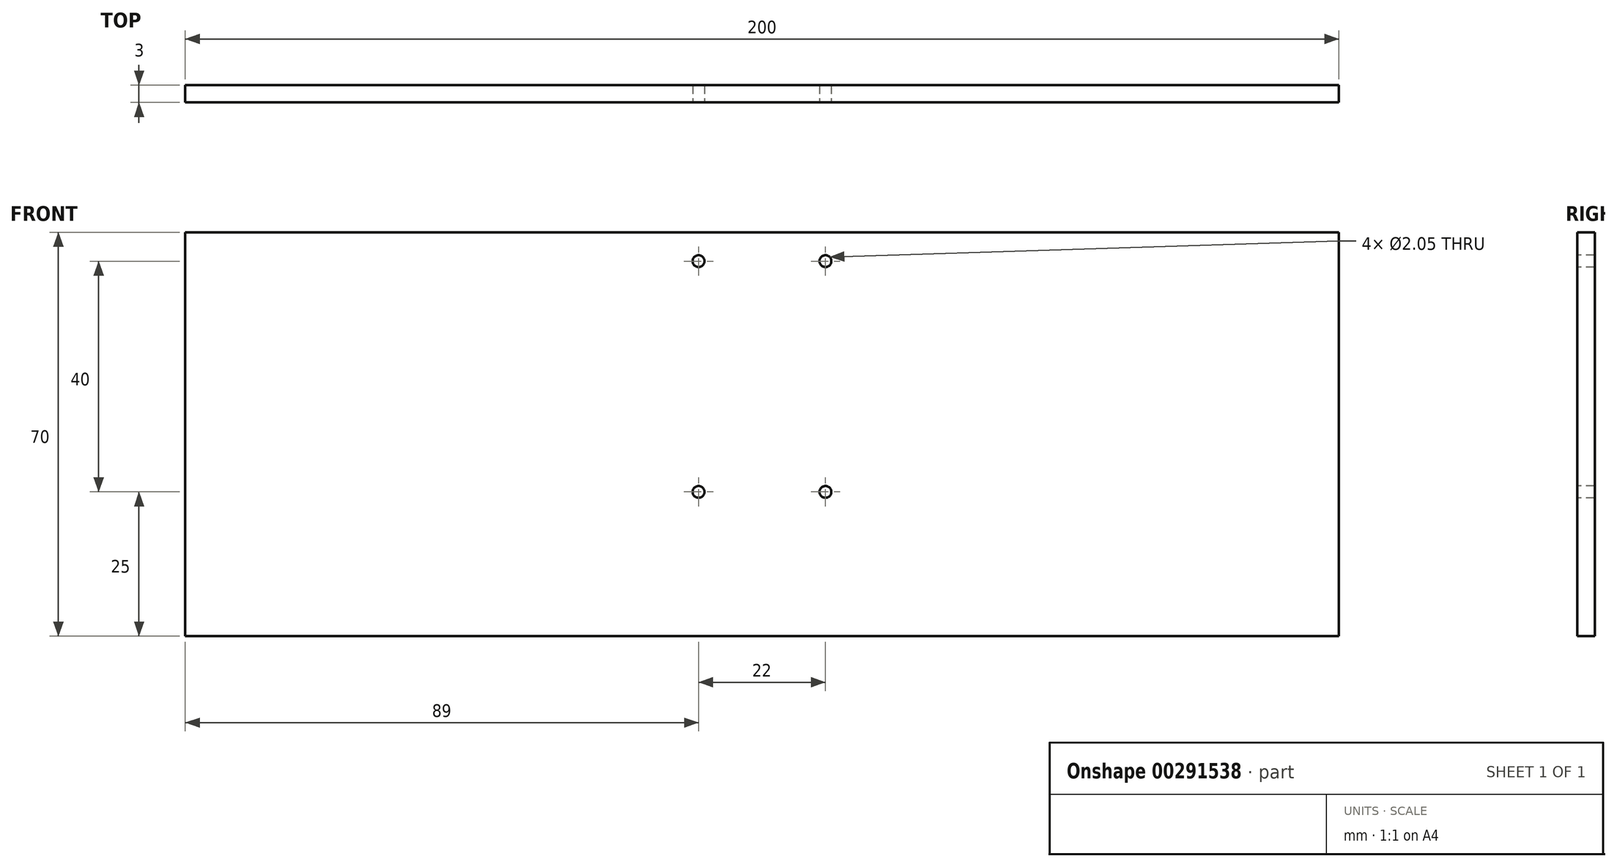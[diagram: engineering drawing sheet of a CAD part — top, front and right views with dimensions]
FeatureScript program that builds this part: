
annotation { "Feature Type Name" : "Feature", "Feature Type Description" : "" }
export const myFeature = defineFeature(function(context is Context, id is Id, definition is map)
    precondition{}
    {
        {
            var Q0;
            Q0=qCreatedBy(makeId("Front.planeOp"),FACE);
            var sketch = newSketch(context, id + "F0", { "sketchPlane" : qUnion([Q0])});
            skLineSegment(sketch, "E0.bottom", {"start": v(-100, 25) * mm, "end": v(100, 25) * mm});
            skLineSegment(sketch, "E0.top", {"start": v(-100, -45) * mm, "end": v(100, -45) * mm});
            skLineSegment(sketch, "E0.left", {"start": v(-100, 25) * mm, "end": v(-100, -45) * mm});
            skLineSegment(sketch, "E0.right", {"start": v(100, 25) * mm, "end": v(100, -45) * mm});
            skSolve(sketch);
        }
        {
            var Q0;
            Q0=makeQuery(id+"F0.imprint","IMPRINT",FACE,{"disambiguationData":[TD([[makeQuery(id+"F0.imprint","IMPRINT",EDGE,{"derivedFrom":sQuery(id+"F0.wireOp",EDGE,"E0.bottom")}),-1.0]])]});
            extrude(context, id + "F1", {"entities" : qUnion([Q0]), "endBound" : BoundingType.SYMMETRIC, "depth" : 3 * mm});
        }
        {
            var Q0;
            Q0=makeQuery(id+"F1.opExtrude","CAP_FACE",FACE,{"disambiguationData":[OSD([sQuery(id+"F0.wireOp",EDGE,"E0.bottom"),sQuery(id+"F0.wireOp",EDGE,"E0.top"),sQuery(id+"F0.wireOp",EDGE,"E0.left"),sQuery(id+"F0.wireOp",EDGE,"E0.right")])],"isStart":false});
            var sketch = newSketch(context, id + "F2", { "sketchPlane" : qUnion([Q0])});
            skCircle(sketch, "E1", {"center": v(-11, 20) * mm, "radius": 1.02 * mm});
            skCircle(sketch, "E2", {"center": v(11, 20) * mm, "radius": 1.02 * mm});
            skCircle(sketch, "E3", {"center": v(11, -20) * mm, "radius": 1.02 * mm});
            skCircle(sketch, "E4", {"center": v(-11, -20) * mm, "radius": 1.02 * mm});
            skSolve(sketch);
        }
        {
            var Q0;
            Q0 = qSketchRegion(id + "F2", true);
            extrude(context, id + "F3", {"entities" : qUnion([Q0]), "operationType" : NewBodyOperationType.REMOVE, "endBound" : BoundingType.UP_TO_NEXT, "oppositeDirection" : true, "depth" : 25 * mm});
        }
    });
